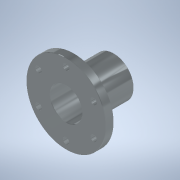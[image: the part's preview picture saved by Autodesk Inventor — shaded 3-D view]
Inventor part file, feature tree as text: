
AUTODESK INVENTOR PART (.ipt)
format: ipt  version: 2020 (Build 240168000, 168)  size: 161,792 bytes
history: native  units: mm
features: sketch x2, revolve x1, hole x1, pattern_circular x1
ambient origin geometry x8: Origin, YZ Plane, XZ Plane, XY Plane, X Axis, Y Axis, Z Axis, Center Point
bodies: Solid1 (feature_tree)
feature tree (5):
  revolve  "Revolution1"  [1 undecoded]
  hole  "Hole1"  [1 undecoded]
  pattern_circular  "Circular Pattern1"  [2 undecoded]
  sketch  "Sketch1"  dims[d0=40.0mm d1=4.0mm]
  sketch  "Sketch2"  dims[d2=20.0mm d6=10.0mm d7=2.0mm d8=20.0mm d9=16.0mm d10=0.2mm d11=0.2mm d12=0.2mm d13=0.2mm d14=0.2mm d15=0.2mm d16=0.2mm d17=0.2mm d18=0.2mm d19=0.2mm d20=90.0deg d21=16.0mm d22=3.2mm d23=6.0mm d24=6.0mm d25=2.0mm d26=90.0deg d27=8.0mm d28=20.594885mm d29=60.0mm d30=360.0deg]
note: 4 required parameter values undecoded (feature->parameter linkage not recoverable at this tier; creation-order binding heuristic only, values carry confidence <= 0.55)